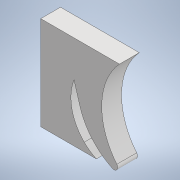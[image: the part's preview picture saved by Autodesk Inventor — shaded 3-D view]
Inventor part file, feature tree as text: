
AUTODESK INVENTOR PART (.ipt)
format: ipt  version: 2022 (Build 260153000, 153)  size: 116,224 bytes
history: native  units: in
note: dims shown in document units (in); Inventor stores cm internally (conversion verified against a paired STEP export)
features: sketch x2, sheet_metal_op x1, other x1
ambient origin geometry x8: Origin, YZ Plane, XZ Plane, XY Plane, X Axis, Y Axis, Z Axis, Center Point
bodies: Solid1 (feature_tree)
feature tree (4):
  sketch  "Sketch1"  dims[d0=0.0591in]
  sheet_metal_op  "Face1"
  sketch  "Sketch2"
  other  "Plate1"
